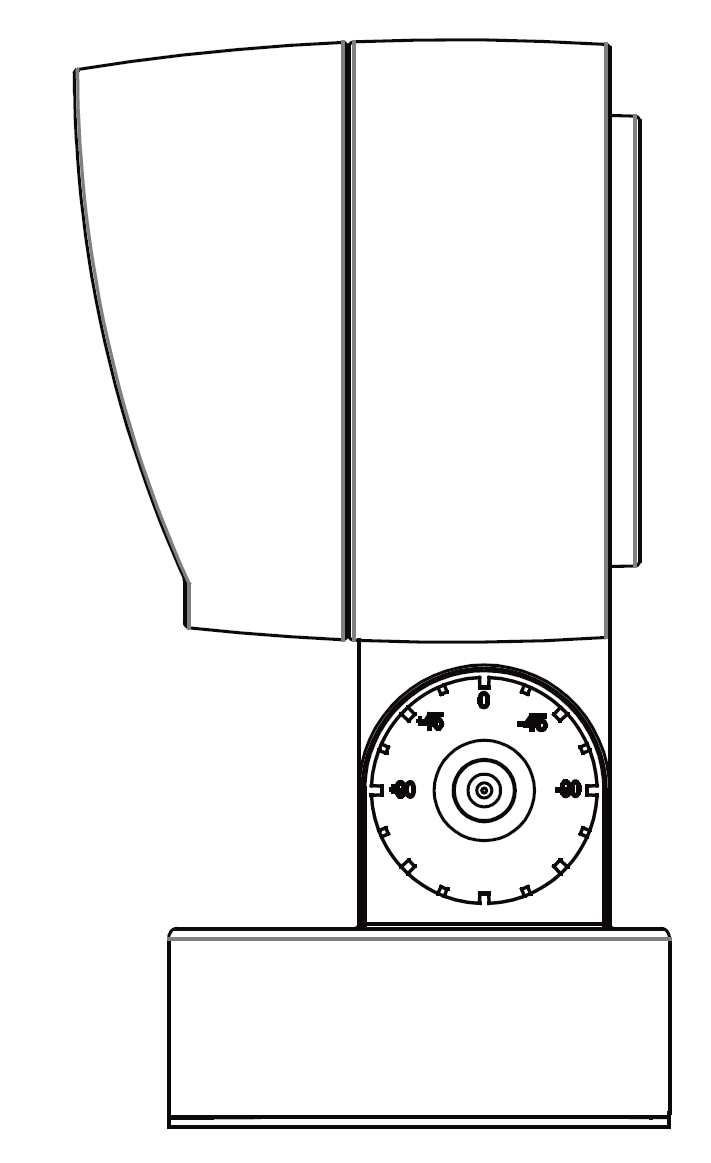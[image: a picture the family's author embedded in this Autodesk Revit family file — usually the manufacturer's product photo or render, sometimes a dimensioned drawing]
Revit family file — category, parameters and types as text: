
# Revit family: Holly Flood Light_42W_3000K
name_source: partatom
category: Lighting Fixtures
units: mm (PartAtom-declared; Revit-internal decimal feet)

## family parameters
Always vertical = Yes
Cut with Voids When Loaded = No
Light Source = No
Maintain Annotation Orientation = No
Part Type = Normal
Room Calculation Point = No
Round Connector Dimension = Use Diameter
Shared = No
Work Plane-Based = No

## types (5) — shared parameters
Assembly Code = HOLLY Flood Light - Canopy Cover
CCT = 3000K
CRI = 80
Default Elevation = 0' - 0"
Height = 0' - 10 15/32"
IP Rating = 65
Input Voltage = 120-277V
Lamp = LED
Load Classification = Lighting
Manufacturer = Above All Lighting
Power Factor = 0.9
URL = https://www.abovealllighting.com
Wattage Comments = 42W
Width = 0' - 7 3/32"

## per-type parameters (varying)
| type | Beam Angle | Delivered Lumen | Light Source | Model |
| Holly Flood _42w_3000K_50° | 50.00° | 4000 lx | 42W-Tiltable : Holly Flood_42W_3000K_50° | HOFL_C42301_50 |
| Holly Flood _42w_3000K_36° | 36.00° | 4000 lx | 42W-Tiltable : Holly Flood_42W_3000K_36° | HOFL_C42301_36 |
| Holly Flood _42w_3000K_24° | 24.00° | 4000 lx | 42W-Tiltable : Holly Flood_42W_3000K_24° | HOFL_C42301_24 |
| Holly Flood _42w_3000K_15° | 15.00° | 4000 lx | 42W-Tiltable : Holly Flood_42W_3000K_15° | HOFL_C42301_15 |
| Holly Flood _42w_3000K_5° | 5.00° | 2400 lx | 42W-Tiltable : Holly Flood_42W_3000K_5° | HOFL_C42301_5 |

## geometry (parser evidence)
native form markers: Sweep x18
no freeform markers — native parametric forms only
